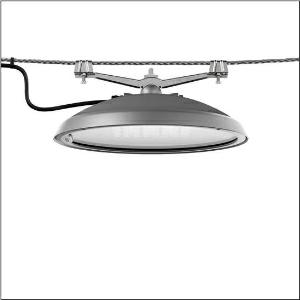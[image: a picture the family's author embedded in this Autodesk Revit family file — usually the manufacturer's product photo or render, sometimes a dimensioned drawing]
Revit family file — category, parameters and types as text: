
# Revit family: dl_r__50_iq_mini___p1_0s_5xa248u31f08ge_4109
name_source: partatom
category: Lighting Fixtures
units: mm (PartAtom-declared; Revit-internal decimal feet)

## family parameters
Cut with Voids When Loaded = No
Host = Face
Light Source = No
Part Type = Normal
Room Calculation Point = No
Round Connector Dimension = Use Diameter
Shared = No

## types (1)
- --- (1 x LED, 5030 lm, 32.7 W, 3000K)
    Apparent Load = 33 VA
    CIE Flux Codes = 23 54 93 100 100
    Color Rendering = 70
    Color Temperature = 3000K
    Default Elevation = 1800 mm
    Description = DL® 50 iQ mini, catenary luminaire, primary light control with lens, of PMMA, primary optical cover: cover, of toughened safety glass, transparent, light distribution: P1.0s, light emission: direct distribution, primary light characteristic: symmetric, installation type: suspended mounting, LED, High Power LED, rated luminous flux: 5.030lm, luminous efficacy: 154lm/W, light colour: 730, colour temperature: 3000K, control: optimised constant luminous flux control (CLO 2.0), Desk-Remote (wireless, voltage-free reading and setting of iQ features in the workshop via application-optimized NFC function/RFID function), Light-Fading, Smart-Wire, Night-Set, Lumen-Switch, Temp-Guard, Auto-Match, Street-Remote, mains connection: 230..240V, AC, 50/60Hz, start of lifetime: 33W, end of service life: 34W, reduction: 16W, luminaire housing, of diecast aluminium, powder-coated, Siteco® metallic grey (DB 702S), diameter: 500mm, height: 115mm, protection rating (complete): IP66, insulation class (complete): insulation class II (safety insulation), certification: CE, ENEC, VDE, impact resistance: IK08, permissible operating ambient temperature for outdoor applications: -25..+40°C, standard-compliant lighting for roads and squares, packaging unit: 1 piece

Light Distribution: P1.0s
    Height = 124 mm  [stored 0.406824 ft]
    Lamp = 1 x LED
    Lamp Light Flux = 5030 lm
    Lamp Power = 32.7 W
    Lamp count = 1
    Length = 500 mm
    Luminous efficacy = 154 lm/W
    Manufacturer = Siteco
    ModVariant = No
    Model = 5XA248U31F08GE
    Number of Poles = 1
    OnlyDefault = Yes
    Power Factor = 1
    Product Name = DL® 50 iQ mini | P1.0s
    Product group = catenary luminaire
    ProductGroupID = 6300
    Protection Class = Protection class II
    Protection Degree = IP 66
    RLX_Detail_Level = 1
    RLX_Emergency_Light_Flux = 0 lm
    RLX_Emergency_Type = 0
    RLX_Emergency_Type_DB = No
    RlxData = <blob elided: 123157 chars, md5=eedf2f8e>
    Socket = socket
    Standby Power = 0 W
    System Light Flux = 5030 lm
    System Power = 33 W
    Type Comments = factory setting: luminous flux: 100 % | dim-lin: 254 | 340 mA
    Type Image = l_1242791.jpg
    URL = http://relux.com
    VarID = @adj_089591
    Voltage = 0 V
    Weight = 0.00 kg
    Width = 0 mm  [stored 0 ft]

note: [stored X ft] marks values corroborated as IEEE doubles in the binary element streams (Revit-internal decimal feet)

## geometry (parser evidence)
native form markers: Blend x4, Sweep x11
no freeform markers — native parametric forms only
